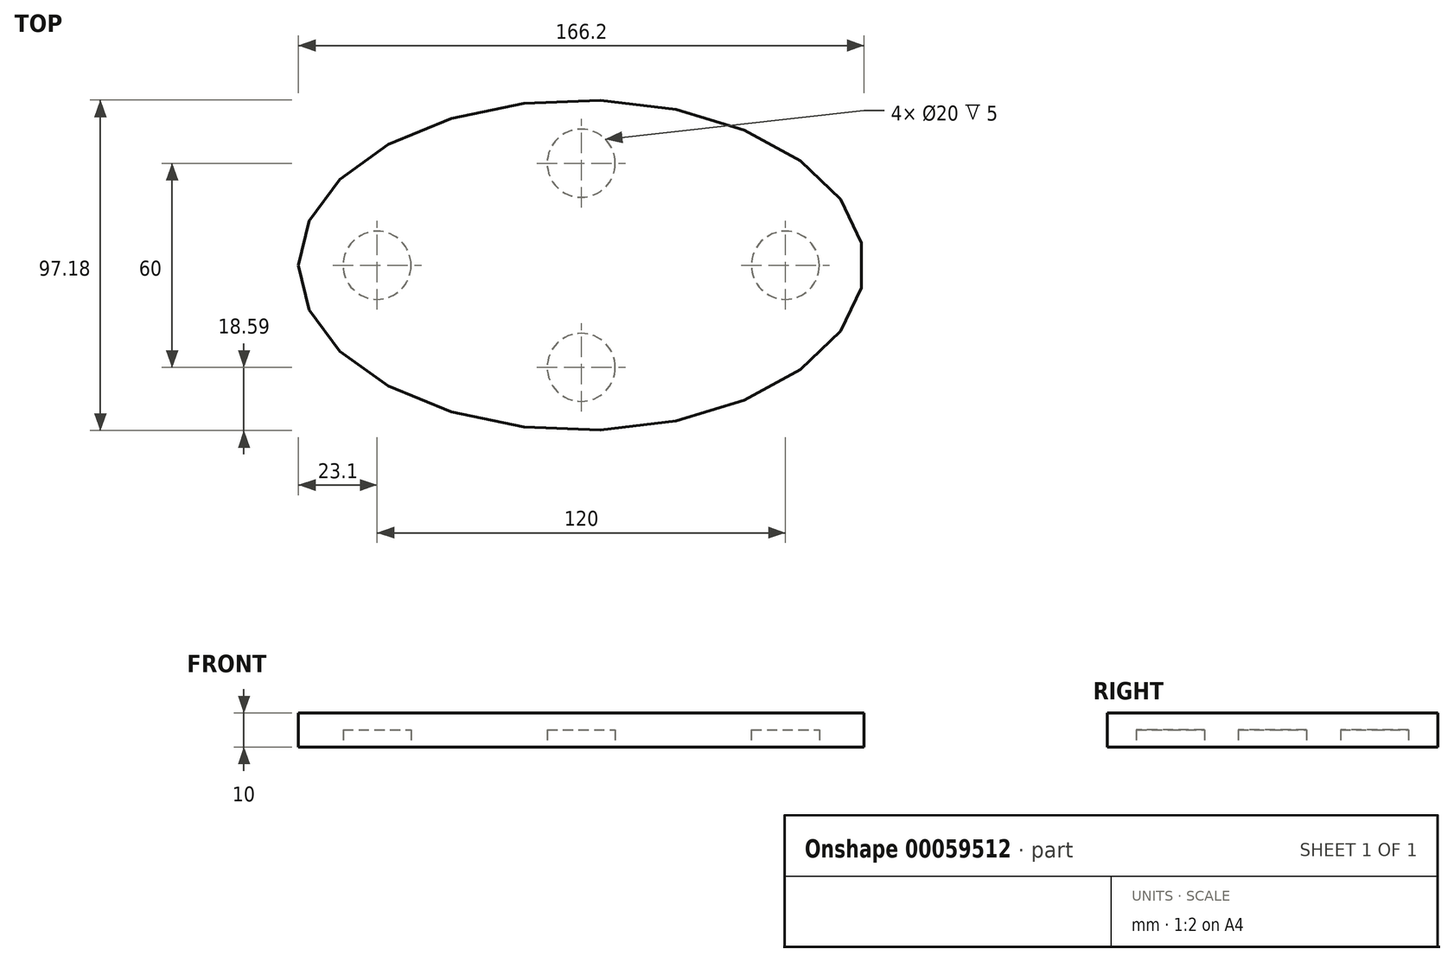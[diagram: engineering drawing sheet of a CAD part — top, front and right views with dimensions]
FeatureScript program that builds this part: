
annotation { "Feature Type Name" : "Feature", "Feature Type Description" : "" }
export const myFeature = defineFeature(function(context is Context, id is Id, definition is map)
    precondition{}
    {
        {
            var Q0;
            Q0=qCreatedBy(makeId("Top.planeOp"),FACE);
            var sketch = newSketch(context, id + "F0", { "sketchPlane" : qUnion([Q0])});
            skEllipse(sketch, "E0", {"center": v(0, 0) * mm, "majorRadius": 83.1 * mm, "minorRadius": 48.59 * mm, "majorAxis": v(-1, 0)});
            skSolve(sketch);
        }
        {
            var Q0;
            Q0=makeQuery(id+"F0.imprint","IMPRINT",FACE,{"disambiguationData":[TD([[makeQuery(id+"F0.imprint","IMPRINT",EDGE,{"derivedFrom":sQuery(id+"F0.wireOp",EDGE,"E0")}),1.0]])]});
            extrude(context, id + "F1", {"entities" : qUnion([Q0]), "depth" : 10 * mm});
        }
        {
            var Q0;
            Q0=makeQuery(id+"F1.opExtrude","CAP_FACE",FACE,{"disambiguationData":[OSD([sQuery(id+"F0.wireOp",EDGE,"E0")])],"isStart":true});
            var sketch = newSketch(context, id + "F2", { "sketchPlane" : qUnion([Q0])});
            skCircle(sketch, "E1", {"center": v(0, 30) * mm, "radius": 10 * mm});
            skCircle(sketch, "E2", {"center": v(-60, 0) * mm, "radius": 10 * mm});
            skCircle(sketch, "E3.MirrorC", {"center": v(0, -30) * mm, "radius": 10 * mm});
            skCircle(sketch, "E4.MirrorC", {"center": v(60, 0) * mm, "radius": 10 * mm});
            skSolve(sketch);
        }
        {
            var Q0;
            Q0 = qSketchRegion(id + "F2", true);
            extrude(context, id + "F3", {"entities" : qUnion([Q0]), "operationType" : NewBodyOperationType.REMOVE, "oppositeDirection" : true, "depth" : 5 * mm});
        }
    });
